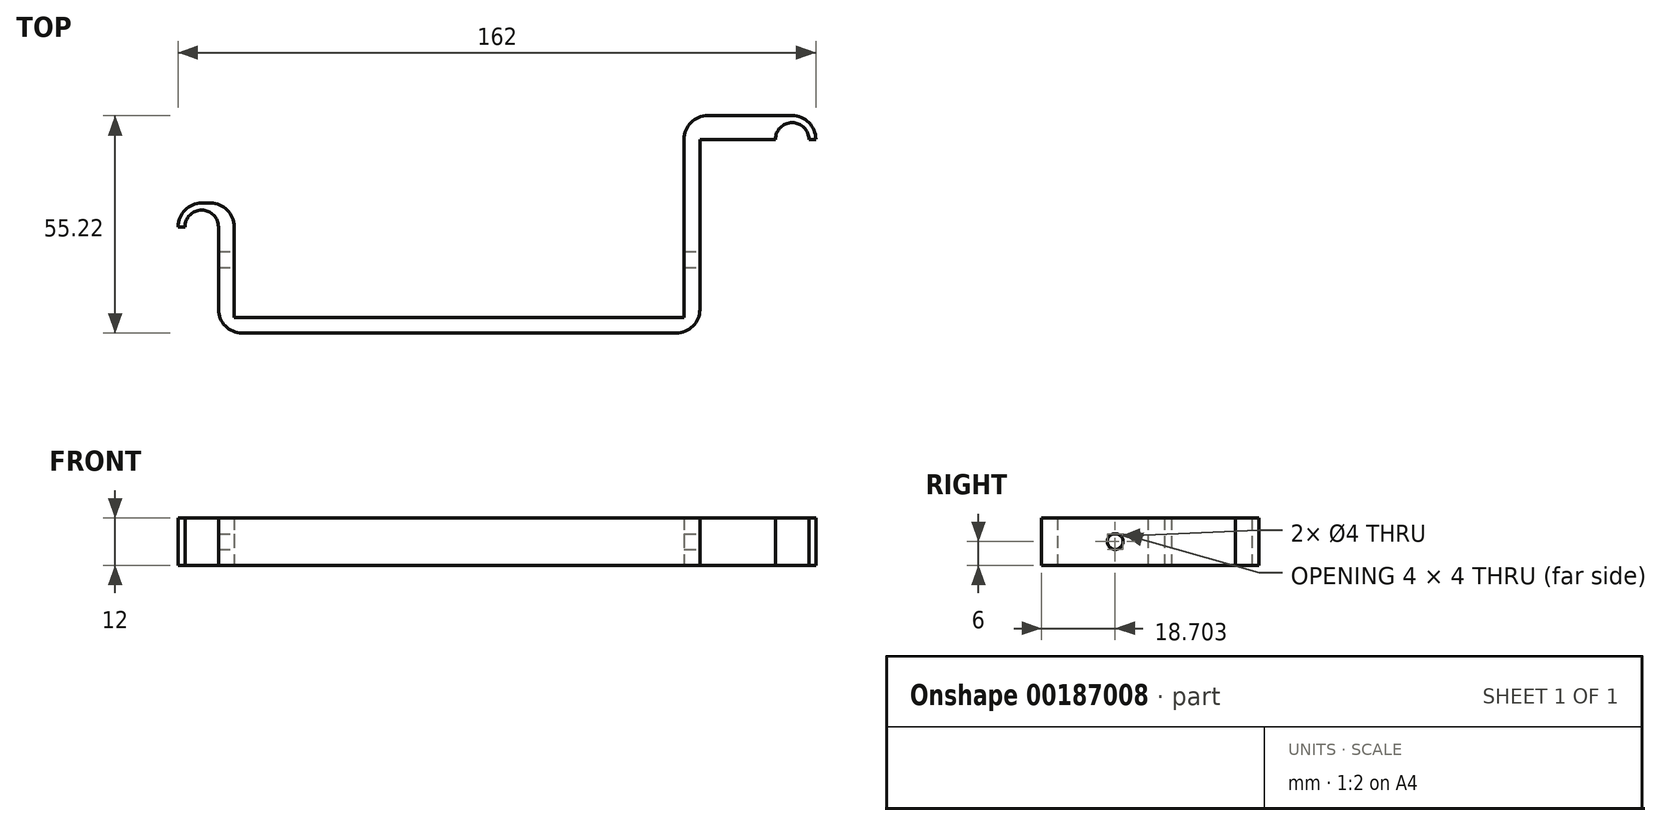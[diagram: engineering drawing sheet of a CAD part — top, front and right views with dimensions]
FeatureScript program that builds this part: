
annotation { "Feature Type Name" : "Feature", "Feature Type Description" : "" }
export const myFeature = defineFeature(function(context is Context, id is Id, definition is map)
    precondition{}
    {
        {
            var Q0;
            Q0=qCreatedBy(makeId("Top.planeOp"),FACE);
            var sketch = newSketch(context, id + "F0", { "sketchPlane" : qUnion([Q0])});
            skArc(sketch, "E0", {"start": v(4.25, 0) * mm, "mid": v(0, 4.25) * mm, "end": v(-4.25, 0) * mm});
            skArc(sketch, "E1", {"start": v(154.25, 22.23) * mm, "mid": v(150, 26.48) * mm, "end": v(145.75, 22.23) * mm});
            skLineSegment(sketch, "E2", {"start": v(57.36, -26.99) * mm, "end": v(-55.73, -26.99) * mm, "construction": true});
            skLineSegment(sketch, "E3", {"start": v(8.25, -22.99) * mm, "end": v(8.25, 0) * mm});
            skLineSegment(sketch, "E4", {"start": v(2.25, 6) * mm, "end": v(0, 6) * mm});
            skLineSegment(sketch, "E5", {"start": v(-6, 0) * mm, "end": v(-4.25, 0) * mm});
            skLineSegment(sketch, "E6", {"start": v(4.25, 0) * mm, "end": v(4.25, 0) * mm});
            skLineSegment(sketch, "E7", {"start": v(4.25, 0) * mm, "end": v(4.25, -20.99) * mm});
            skLineSegment(sketch, "E8", {"start": v(10.25, -26.99) * mm, "end": v(120.55, -26.99) * mm});
            skLineSegment(sketch, "E9", {"start": v(8.25, -22.99) * mm, "end": v(122.55, -22.99) * mm});
            skLineSegment(sketch, "E10", {"start": v(122.55, -22.99) * mm, "end": v(122.55, 22.23) * mm});
            skLineSegment(sketch, "E11", {"start": v(126.55, 22.23) * mm, "end": v(126.55, -20.99) * mm});
            skLineSegment(sketch, "E12", {"start": v(128.55, 28.23) * mm, "end": v(150, 28.23) * mm});
            skLineSegment(sketch, "E13", {"start": v(154.25, 22.23) * mm, "end": v(156, 22.23) * mm});
            skLineSegment(sketch, "E14", {"start": v(145.75, 22.23) * mm, "end": v(126.55, 22.23) * mm});
            skArc(sketch, "E15", {"start": v(156, 22.23) * mm, "mid": v(154.24, 26.47) * mm, "end": v(150, 28.23) * mm});
            skArc(sketch, "E16", {"start": v(-6, 0) * mm, "mid": v(-4.24, 4.24) * mm, "end": v(0, 6) * mm});
            skPoint(sketch, "E17.visualSharp", {"position": v(122.55, 28.23) * mm});
            skArc(sketch, "E17.filletArc", {"start": v(128.55, 28.23) * mm, "mid": v(124.3, 26.47) * mm, "end": v(122.55, 22.23) * mm});
            skPoint(sketch, "E18.visualSharp", {"position": v(126.55, -26.99) * mm});
            skArc(sketch, "E18.filletArc", {"start": v(120.55, -26.99) * mm, "mid": v(124.8, -25.23) * mm, "end": v(126.55, -20.99) * mm});
            skPoint(sketch, "E19.visualSharp", {"position": v(4.25, -26.99) * mm});
            skArc(sketch, "E19.filletArc", {"start": v(4.25, -20.99) * mm, "mid": v(6, -25.23) * mm, "end": v(10.25, -26.99) * mm});
            skPoint(sketch, "E20.visualSharp", {"position": v(8.25, 6) * mm});
            skArc(sketch, "E20.filletArc", {"start": v(8.25, 0) * mm, "mid": v(6.5, 4.24) * mm, "end": v(2.25, 6) * mm});
            skSolve(sketch);
        }
        {
            var Q0;
            Q0 = qSketchRegion(id + "F0", true);
            extrude(context, id + "F1", {"entities" : qUnion([Q0]), "depth" : 12 * mm});
        }
        {
            var Q0;
            Q0=makeQuery(id+"F1.opExtrude","SWEPT_FACE",FACE,{"disambiguationData":[OSD([sQuery(id+"F0.wireOp",EDGE,"E11")])]});
            var sketch = newSketch(context, id + "F2", { "sketchPlane" : qUnion([Q0])});
            skCircle(sketch, "E21", {"center": v(-8.29, 6) * mm, "radius": 2 * mm});
            skPoint(sketch, "E21.centerSnap0", {"position": v(-20.99, 6) * mm});
            skSolve(sketch);
        }
        {
            var Q0;
            Q0 = qSketchRegion(id + "F2", true);
            extrude(context, id + "F3", {"entities" : qUnion([Q0]), "operationType" : NewBodyOperationType.REMOVE, "endBound" : BoundingType.THROUGH_ALL, "oppositeDirection" : true, "depth" : 25 * mm});
        }
    });
